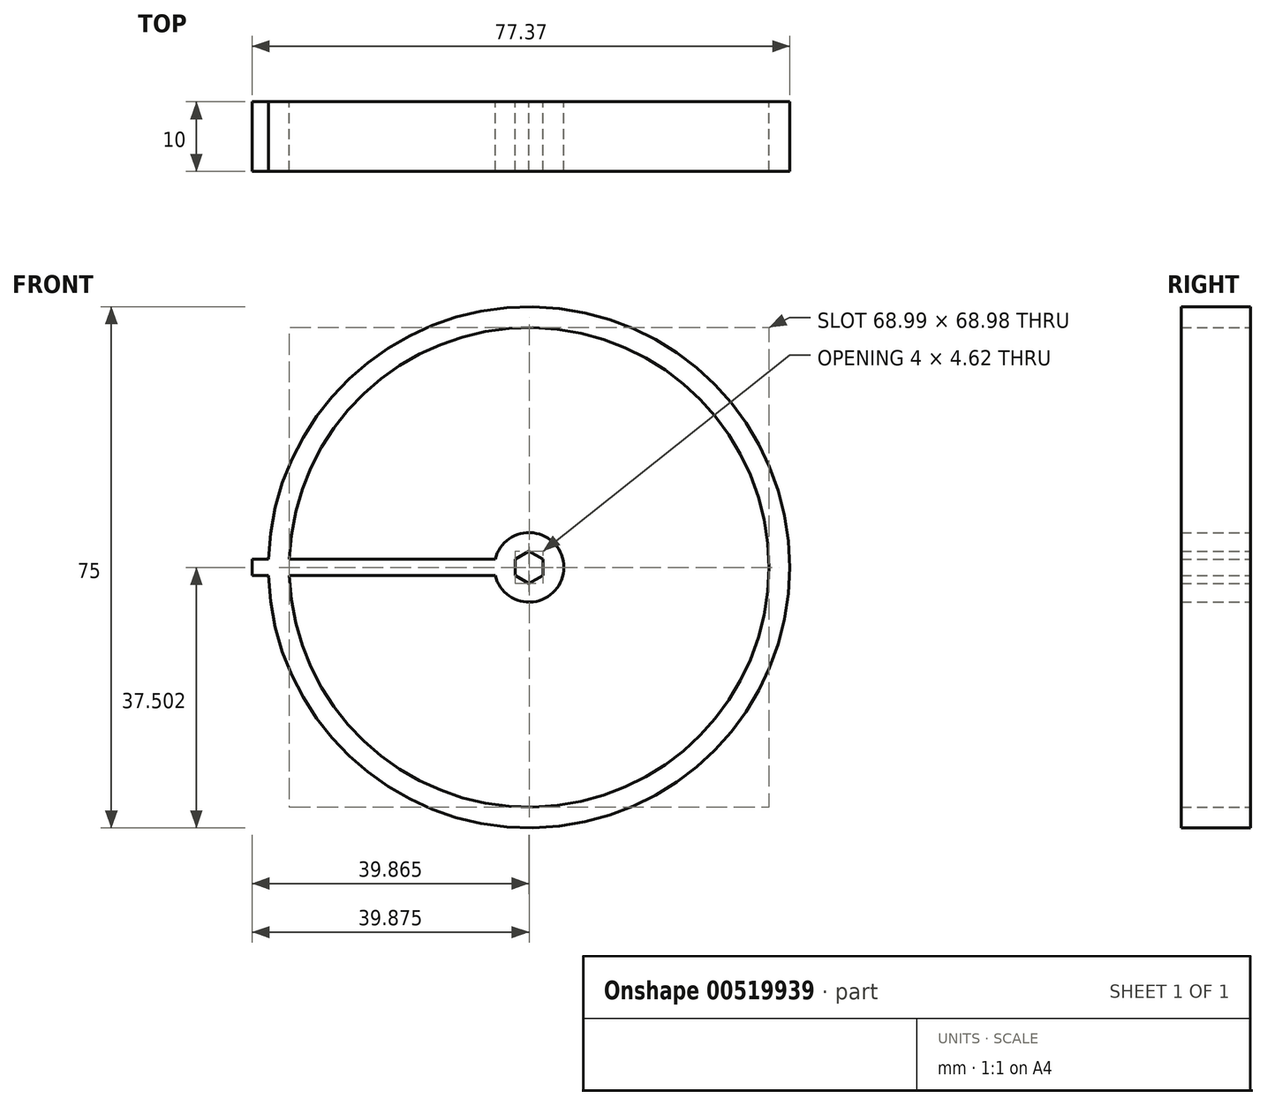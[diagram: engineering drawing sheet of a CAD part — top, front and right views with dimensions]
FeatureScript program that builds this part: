
annotation { "Feature Type Name" : "Feature", "Feature Type Description" : "" }
export const myFeature = defineFeature(function(context is Context, id is Id, definition is map)
    precondition{}
    {
        {
            var Q0;
            Q0=qCreatedBy(makeId("Front.planeOp"),FACE);
            var sketch = newSketch(context, id + "F0", { "sketchPlane" : qUnion([Q0])});
            skCircle(sketch, "E0", {"center": v(59.37, 10.9) * mm, "radius": 37.5 * mm});
            skCircle(sketch, "E1", {"center": v(59.37, 10.9) * mm, "radius": 34.5 * mm});
            skLineSegment(sketch, "E2", {"start": v(62.83, 11.83) * mm, "end": v(62.83, 11.83) * mm});
            skArc(sketch, "E3", {"start": v(54.5, 9.75) * mm, "mid": v(64.37, 10.9) * mm, "end": v(54.5, 12.06) * mm});
            skCircle(sketch, "E4.cCircle", {"center": v(59.37, 10.9) * mm, "radius": 2 * mm, "construction": true});
            skLineSegment(sketch, "E4.0", {"start": v(61.37, 12.06) * mm, "end": v(61.37, 9.75) * mm});
            skLineSegment(sketch, "E4.1", {"start": v(61.37, 9.75) * mm, "end": v(59.37, 8.6) * mm});
            skLineSegment(sketch, "E4.2", {"start": v(59.37, 8.6) * mm, "end": v(57.37, 9.75) * mm});
            skLineSegment(sketch, "E4.3", {"start": v(57.37, 9.75) * mm, "end": v(57.37, 12.06) * mm});
            skLineSegment(sketch, "E4.4", {"start": v(57.37, 12.06) * mm, "end": v(59.37, 13.21) * mm});
            skLineSegment(sketch, "E4.5", {"start": v(59.37, 13.21) * mm, "end": v(61.37, 12.06) * mm});
            skPoint(sketch, "E4.0.midPoint", {"position": v(61.37, 10.9) * mm});
            skLineSegment(sketch, "E5.bottom", {"start": v(54.5, 12.06) * mm, "end": v(19.5, 12.06) * mm});
            skLineSegment(sketch, "E5.top", {"start": v(54.5, 9.75) * mm, "end": v(19.5, 9.75) * mm});
            skLineSegment(sketch, "E5.right", {"start": v(19.5, 12.06) * mm, "end": v(19.5, 9.75) * mm});
            skSolve(sketch);
        }
        {
            var Q0;
            Q0 = qSketchRegion(id + "F0", true);
            var Q1;
            {var subQ0=sQuery(id+"F0.wireOp",EDGE,"E3");Q1=makeQuery(id+"F0.imprint","IMPRINT",FACE,{"disambiguationData":[TD([[makeQuery(id+"F0.imprint","IMPRINT",EDGE,{"derivedFrom":subQ0}),1.0]])]});}
            extrude(context, id + "F1", {"entities" : qUnion([Q0, Q1]), "endBound" : BoundingType.SYMMETRIC, "depth" : 10 * mm, "offsetDistance" : 25 * mm});
        }
    });
